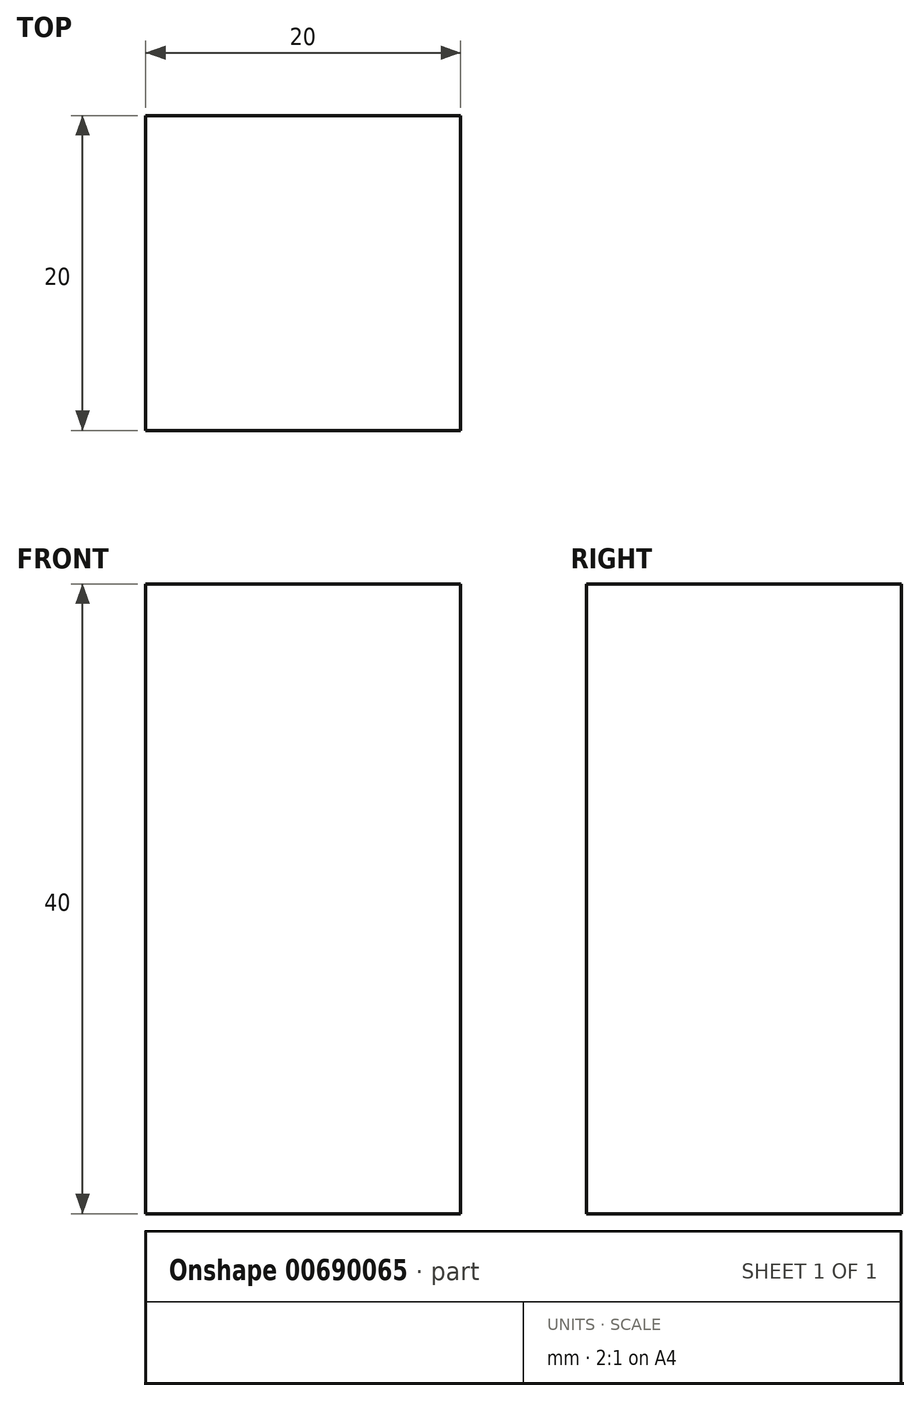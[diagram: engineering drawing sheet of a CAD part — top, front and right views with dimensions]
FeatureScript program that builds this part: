
annotation { "Feature Type Name" : "Feature", "Feature Type Description" : "" }
export const myFeature = defineFeature(function(context is Context, id is Id, definition is map)
    precondition{}
    {
        {
            var Q0;
            Q0=qCreatedBy(makeId("Top.planeOp"),FACE);
            var sketch = newSketch(context, id + "F0", { "sketchPlane" : qUnion([Q0])});
            skLineSegment(sketch, "E0.bottom", {"start": v(10, -10) * mm, "end": v(-10, -10) * mm});
            skLineSegment(sketch, "E0.top", {"start": v(10, 10) * mm, "end": v(-10, 10) * mm});
            skLineSegment(sketch, "E0.left", {"start": v(10, -10) * mm, "end": v(10, 10) * mm});
            skLineSegment(sketch, "E0.right", {"start": v(-10, -10) * mm, "end": v(-10, 10) * mm});
            skPoint(sketch, "E0.middle", {"position": v(0, 0) * mm});
            skSolve(sketch);
        }
        {
            var Q0;
            Q0=makeQuery(id+"F0.imprint","IMPRINT",FACE,{"disambiguationData":[TD([[makeQuery(id+"F0.imprint","IMPRINT",EDGE,{"derivedFrom":sQuery(id+"F0.wireOp",EDGE,"E0.bottom")}),-1.0]])]});
            extrude(context, id + "F1", {"entities" : qUnion([Q0]), "depth" : 40 * mm, "offsetDistance" : 25 * mm});
        }
    });
